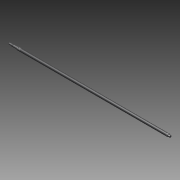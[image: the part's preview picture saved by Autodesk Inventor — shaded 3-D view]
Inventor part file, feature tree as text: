
AUTODESK INVENTOR PART (.ipt)
format: ipt  version: 2016 (Build 200138000, 138)  size: 134,656 bytes
history: native  units: mm
features: other x21, sketch x5, revolve x3, thread x2, extrude x2
ambient origin geometry x8: Origin, YZ Plane, XZ Plane, XY Plane, X Axis, Y Axis, Z Axis, Center Point
bodies: Solid1 (feature_tree)
feature tree (33):
  revolve  "Revolution1"  [1 undecoded]
  thread  "Thread1"  [1 undecoded]
  revolve  "Revolution2"  [1 undecoded]
  thread  "Thread2"  [1 undecoded]
  extrude  "Extrusion1"  TaperAngle=0.0deg  [1 undecoded]
  extrude  "Extrusion2"  [1 undecoded]
  revolve  "Revolution3"  [1 undecoded]
  other  "FSS_XY"
  other  "FSS_YZ"
  other  "FSS_ZX"
  other  "FSS_X"
  other  "FSS_Y"
  other  "FSS_Z"
  other  "FSS_Center"
  other  "SSS_XY"
  other  "SSS_YZ"
  other  "SSS_ZX"
  other  "SSS_X"
  other  "SSS_Y"
  other  "SSS_Z"
  other  "SSS_Center"
  other  "bnt_s_1_XY"
  other  "bnt_s_1_YZ"
  other  "bnt_s_1_ZX"
  other  "bnt_s_1_X"
  other  "bnt_s_1_Y"
  other  "bnt_s_1_Z"
  other  "bnt_s_1_Center"
  sketch  "Sketch_1"  dims[d0=360.0deg d1=1058.0mm d2=0.0mm d3=360.0deg]
  sketch  "Sketch_10"  dims[d4=11.3865mm d5=0.0mm d6=4.0mm d7=0.0mm d8=4.0mm d9=0.0mm]
  sketch  "Sketch_11"  dims[d10=360.0deg d11=0.0mm d12=0.0mm d13=0.0mm]
  sketch  "Sketch_12"
  sketch  "Sketch_16"
note: 7 required parameter values undecoded (feature->parameter linkage not recoverable at this tier; creation-order binding heuristic only, values carry confidence <= 0.55)